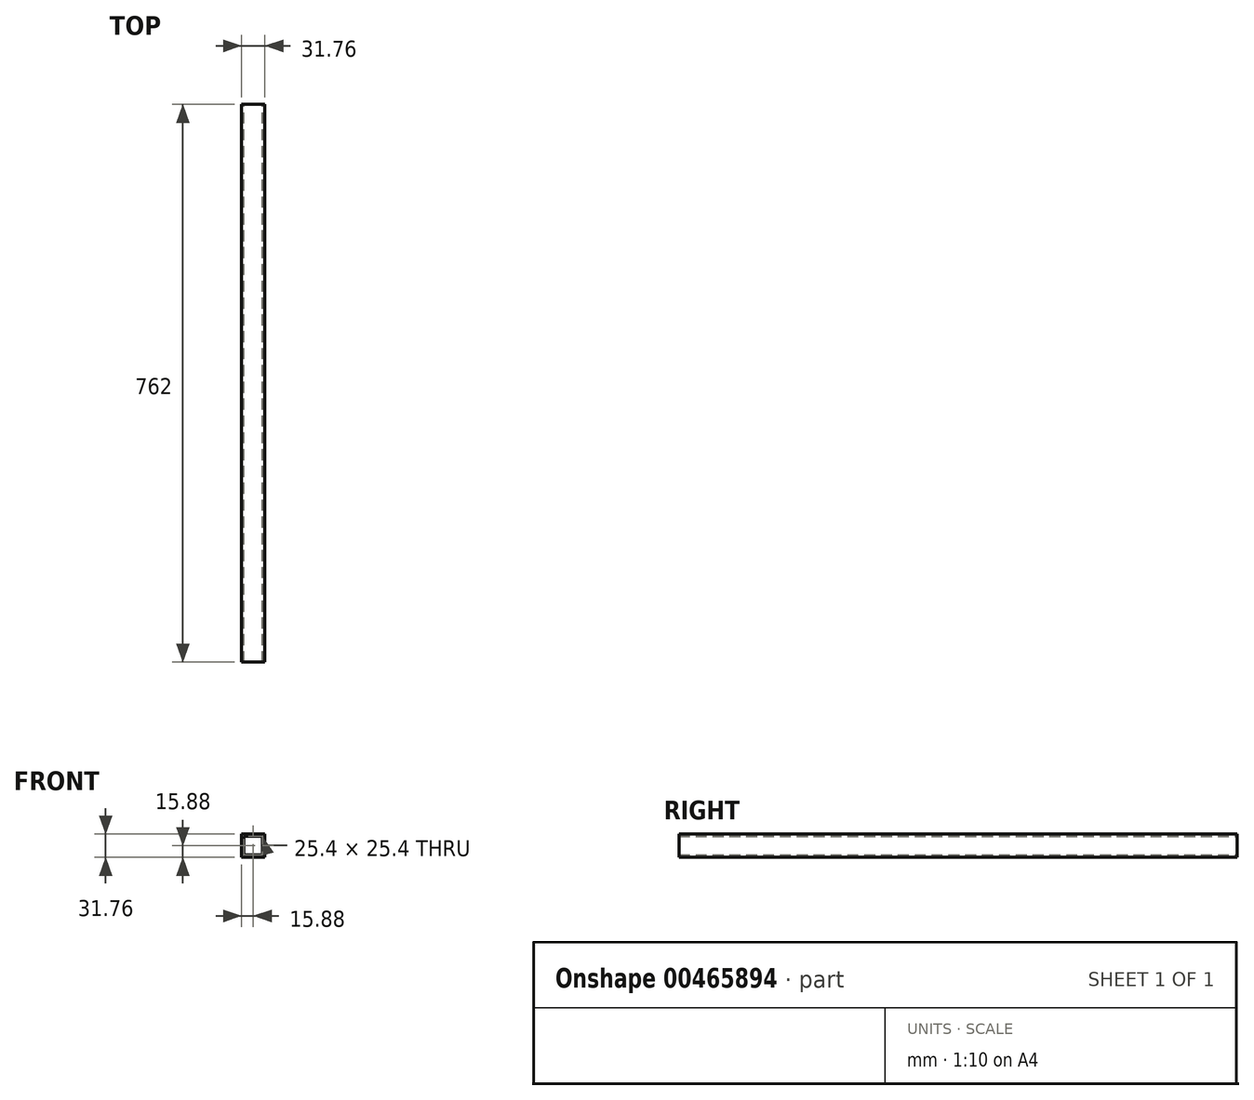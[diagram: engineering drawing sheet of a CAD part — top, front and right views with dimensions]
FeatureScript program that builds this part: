
annotation { "Feature Type Name" : "Feature", "Feature Type Description" : "" }
export const myFeature = defineFeature(function(context is Context, id is Id, definition is map)
    precondition{}
    {
        {
            var Q0;
            Q0=qCreatedBy(makeId("Front.planeOp"),FACE);
            var sketch = newSketch(context, id + "F0", { "sketchPlane" : qUnion([Q0])});
            skLineSegment(sketch, "E0.bottom", {"start": v(-15.87, 15.88) * mm, "end": v(15.88, 15.88) * mm});
            skLineSegment(sketch, "E0.top", {"start": v(-15.88, -15.88) * mm, "end": v(15.87, -15.88) * mm});
            skLineSegment(sketch, "E0.left", {"start": v(-15.87, 15.88) * mm, "end": v(-15.88, -15.88) * mm});
            skLineSegment(sketch, "E0.right", {"start": v(15.88, 15.88) * mm, "end": v(15.87, -15.88) * mm});
            skPoint(sketch, "E0.middle", {"position": v(0, 0) * mm});
            skLineSegment(sketch, "E1.bottom", {"start": v(-12.7, 12.7) * mm, "end": v(12.7, 12.7) * mm});
            skLineSegment(sketch, "E1.top", {"start": v(-12.7, -12.7) * mm, "end": v(12.7, -12.7) * mm});
            skLineSegment(sketch, "E1.left", {"start": v(-12.7, 12.7) * mm, "end": v(-12.7, -12.7) * mm});
            skLineSegment(sketch, "E1.right", {"start": v(12.7, 12.7) * mm, "end": v(12.7, -12.7) * mm});
            skSolve(sketch);
        }
        {
            var Q0;
            Q0=makeQuery(id+"F0.imprint","IMPRINT",FACE,{"disambiguationData":[TD([[makeQuery(id+"F0.imprint","IMPRINT",EDGE,{"derivedFrom":sQuery(id+"F0.wireOp",EDGE,"E0.bottom")}),-1.0]])]});
            extrude(context, id + "F1", {"entities" : qUnion([Q0]), "depth" : 762 * mm});
        }
    });
